# Revit family: FT Pegaso_2020
name_source: partatom
category: Lighting Fixtures
units: mm (PartAtom-declared; Revit-internal decimal feet)

## family parameters
Always vertical = Yes
Cut with Voids When Loaded = No
Light Source = Yes
OmniClass Number = 23.80.70.00
OmniClass Title = Lighting
Part Type = Normal
Room Calculation Point = No
Round Connector Dimension = Use Diameter
Shared = No
Work Plane-Based = No

## types (12) — shared parameters
Chromatic Index = CR>80
Color Filter = 16777215
Description = https://www.airfal.com
Dimming Lamp Color Temperature Shift = <None>
Emergency system = No
Emit from Line Length = 609.6 mm  [stored 2 ft]
Glow wire test = 960ºC
IK = IK10
IP = IP68-2
Led Module = Yes
MacAdam Ellipse = 3/4
Photobiological risk group = RG1
URL = https://www.airfal.com
Unify glade rating = UGR<19
Useful life = L70B50>50000
zero-valued in all types: Default Elevation

## per-type parameters (varying)
| type | L | Net output | Photometric Web File | Size | Tilt Angle | Watts |
| PE113 | 721 mm  [stored 2.36549 ft] | 1084 lm | PE113 PEGASO 600 13W 1490 lm 3000ºK.IES | 673 mm | 60.00° | 13 W |
| PE114 | 721 mm  [stored 2.36549 ft] | 1127 lm | PE114 PEGASO 600 13W 1550 lm 4000ºK.IES | 600 mm | 60.00° | 13 W |
| PE123 | 721 mm  [stored 2.36549 ft] | 1862 lm | PE123 PEGASO 600 16W 2560 lm 3000ºK.IES | 600 mm | 90.00° | 16 W |
| PE124 | 721 mm  [stored 2.36549 ft] | 1942 lm | PE124 PEGASO 600 16W 2670 lm 4000ºK.IES | 600 mm | 90.00° | 16 W |
| PE213 | 1235 mm  [stored 4.05184 ft] | 2168 lm | PE213 PEGASO 1200 24W 2980 lm 3000ºK.IES | 1200 mm | 60.00° | 24 W |
| PE214 | 1235 mm  [stored 4.05184 ft] | 2328 lm | PE214 PEGASO 1200 24W 3200 lm 4000ºK.IES | 1200 mm | 60.00° | 24 W |
| PE223 | 1235 mm  [stored 4.05184 ft] | 3724 lm | PE223 PEGASO 1200 32W 5120 lm 3000ºK.IES | 1200 mm | 90.00° | 32 W |
| PE313 | 1581 mm  [stored 5.18701 ft] | 2706 lm | PE313 PEGASO 1500 29W 3720 lm 3000ºK.IES | 1500 mm  [stored 4.92126 ft] | 60.00° | 29 W |
| PE224 | 1235 mm  [stored 4.05184 ft] | 3884 lm | PE224 PEGASO 1200 32W 5340 lm 4000ºK.IES | 1200 mm | 90.00° | 32 W |
| PE314 | 1581 mm  [stored 5.18701 ft] | 2910 lm | PE314 PEGASO 1500 29W 4000 lm 4000ºK.IES | 1500 mm  [stored 4.92126 ft] | 60.00° | 29 W |
| PE323 | 1581 mm  [stored 5.18701 ft] | 4590 lm | PE323 PEGASO 1500 40W 6310 lm 3000ºK.IES | 1500 mm  [stored 4.92126 ft] | 90.00° | 40 W |
| PE324 | 1581 mm  [stored 5.18701 ft] | 4874 lm | PE324 PEGASO 1500 40W 6700 lm 4000ºK.IES | 1500 mm  [stored 4.92126 ft] | 90.00° | 40 W |

note: [stored X ft] marks values corroborated as IEEE doubles in the binary element streams (Revit-internal decimal feet)

## geometry (parser evidence)
native form markers: Blend x8, Sweep x25
no freeform markers — native parametric forms only
